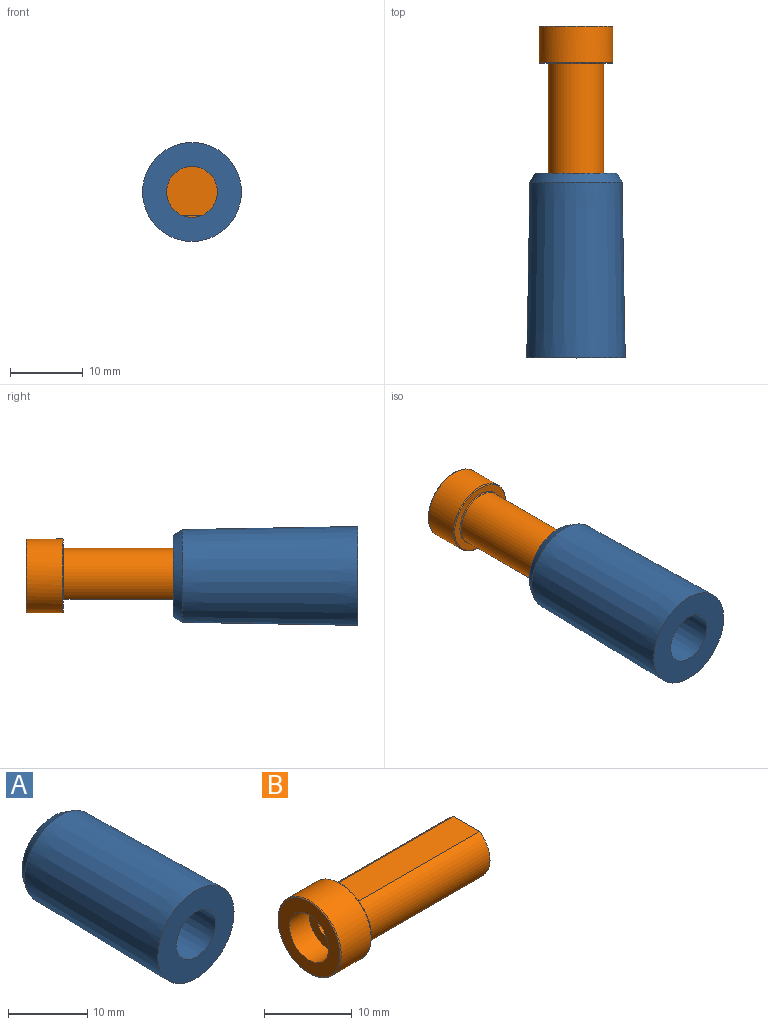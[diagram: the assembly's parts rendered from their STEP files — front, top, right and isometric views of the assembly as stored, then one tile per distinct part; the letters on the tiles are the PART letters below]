
ASSEMBLY  parts=2 mates=1
PART A: 6 faces, bbox 13.6x25.4x13.6 mm
  f0: cone r=3.94mm half-angle=1deg, axis (0,1,0), area 589.9mm2, adj f2,f5
  f1: cone r=6.35mm half-angle=1deg, axis (0,-1,0), area 998.2mm2, adj f2,f4
  f2: plane 13.59x13.59mm, normal (0,-1,0), area 106.6mm2, adj f0,f1
  f3: plane 11.22x11.22mm, normal (0,1,0), area 47mm2, adj f4,f5
  f4: cone r=6.37mm half-angle=31deg, axis (0,-1,0), area 55.8mm2, adj f1,f3
  f5: torus R=4.06mm, axis (0,-1,0), area 4.9mm2, adj f0,f3
PART B: 13 faces, bbox 25.4x11x11 mm
  f0: plane 7.62x6.99mm, normal (1,0,0), area 43.8mm2, adj f1,f8
  f1: cylinder r=3.81mm len=20.19mm, axis (-1,0,0), area 393.3mm2, adj f0,f5,f8
  f2: plane 9.91x9.91mm, normal (1,0,0), area 30.8mm2, adj f5,f6,f8
  f3: cylinder r=5.08mm len=10.16mm, axis (-1,0,0), area 154mm2, adj f6,f7
  f4: plane 9.91x9.91mm, normal (-1,0,0), area 45.4mm2, adj f7,f11
  f5: torus R=3.94mm, axis (1,0,0), area 3.9mm2, adj f1,f2,f8
  f6: torus R=4.95mm, axis (1,0,0), area 6.3mm2, adj f2,f3
  f7: torus R=4.95mm, axis (-1,0,0), area 6.3mm2, adj f3,f4
  f8: plane 20.32x4.66mm, normal (0,0,1), area 85.6mm2, adj f0,f1,f2,f5
  f9: cylinder r=1.79mm len=5.72mm, axis (-1,0,0), area 64.3mm2, adj f10,f12
  f10: plane 6.35x6.35mm, normal (-1,0,0), area 21.6mm2, adj f9,f11
  f11: cylinder r=3.17mm len=6.35mm, axis (-1,0,0), area 63.3mm2, adj f4,f10
  f12: cone r=0mm half-angle=59deg, axis (-1,0,0), area 11.8mm2, adj f9
PLACE A t=(0.14,12.73,-0.07)mm fixed
PLACE B rot(axis=(0.71,-0.71,0),180deg) t=(0.14,32.94,-0.07)mm
MATE slider B.f1 <-> A.f1  axis (0,1,0) through (0.14,27.73,-0.07)mm
